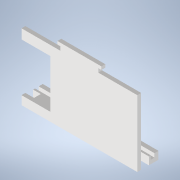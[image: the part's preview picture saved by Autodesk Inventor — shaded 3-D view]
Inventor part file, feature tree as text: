
AUTODESK INVENTOR PART (.ipt)
format: ipt  version: 2022.2 (Build 262287000, 287)  size: 160,768 bytes
history: native  units: mm
features: extrude x5, sketch x5
ambient origin geometry x8: Origin, YZ Plane, XZ Plane, XY Plane, X Axis, Y Axis, Z Axis, Center Point
bodies: Volumenkörper1 (feature_tree)
feature tree (10):
  extrude  "Extrusion1"  Depth=19.6mm
  extrude  "Extrusion2"  Depth=1.6mm
  extrude  "Extrusion3"  Depth=1.6mm
  extrude  "Extrusion4"  Depth=60.0mm
  extrude  "Extrusion5"  Depth=9.8mm
  sketch  "Skizze1"  dims[d0=3.6mm d1=19.6mm]
  sketch  "Skizze2"  dims[d2=1.6mm d3=1.6mm]
  sketch  "Skizze3"  dims[d4=1.6mm d5=1.6mm]
  sketch  "Skizze4"  dims[d6=34.5mm d7=60.0mm]
  sketch  "Skizze5"  dims[d8=30.0mm d9=9.8mm d10=2.0mm d11=0.0mm d12=4.0mm d13=9.0mm d14=0.0mm d15=1.9mm d16=2.0mm d17=5.0mm d18=0.0mm d19=0.0mm d20=4.0mm d21=4.0mm d22=4.0mm d23=4.0mm d24=10.0mm d25=0.0mm d28=15.0mm d29=25.0mm d30=5.0mm d31=10.0mm d32=0.0mm]
